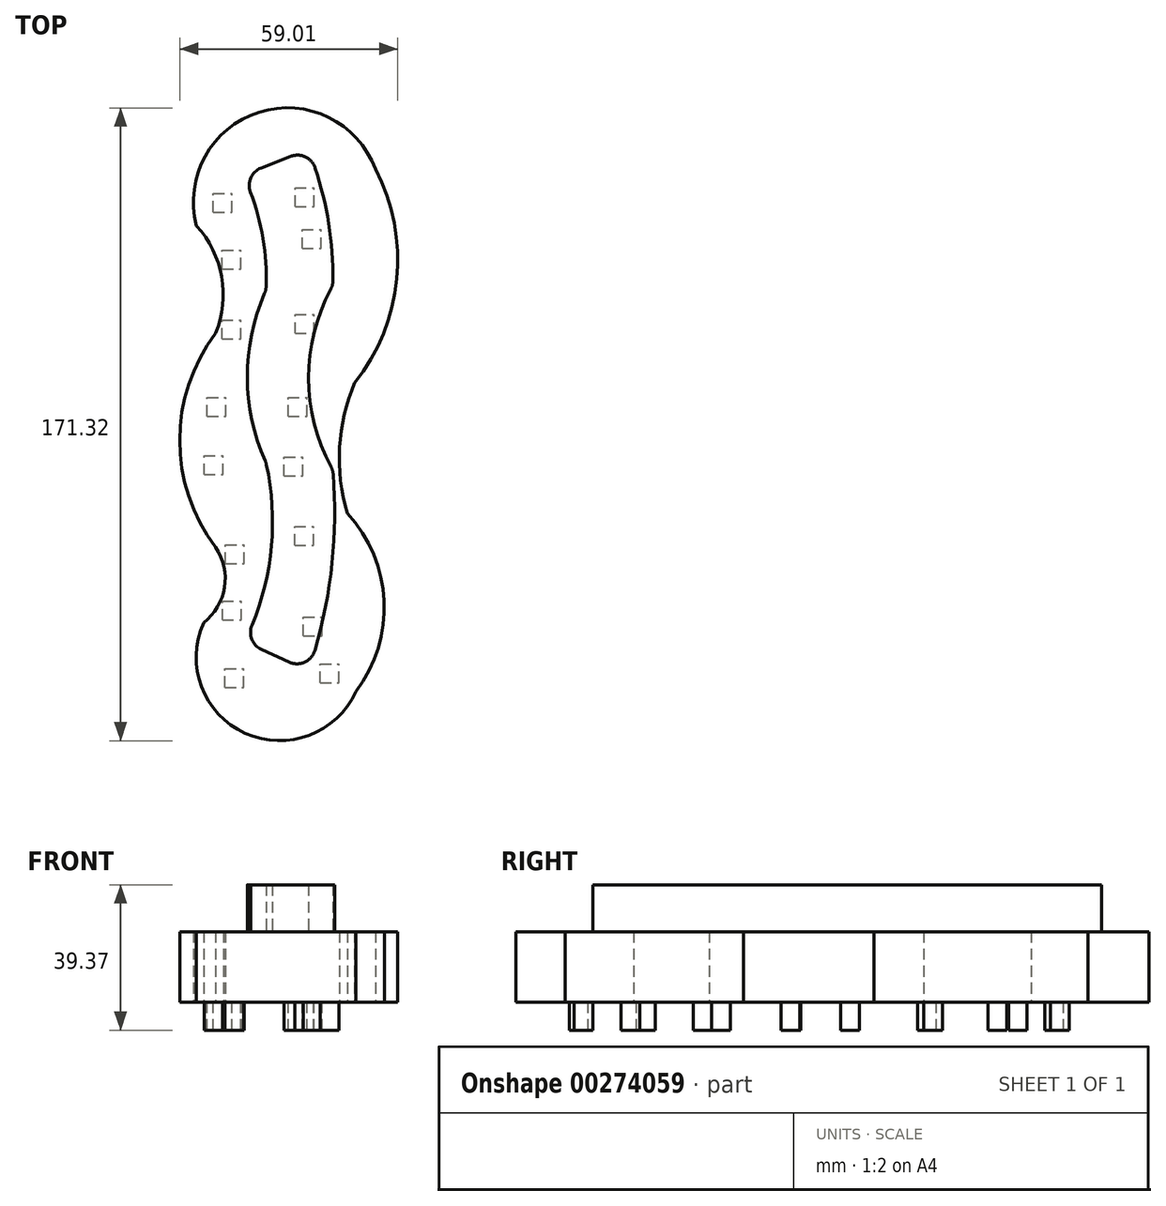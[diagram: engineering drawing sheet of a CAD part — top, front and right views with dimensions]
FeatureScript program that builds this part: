
annotation { "Feature Type Name" : "Feature", "Feature Type Description" : "" }
export const myFeature = defineFeature(function(context is Context, id is Id, definition is map)
    precondition{}
    {
        {
            var Q0;
            Q0=qCreatedBy(makeId("Top.planeOp"),FACE);
            var sketch = newSketch(context, id + "F0", { "sketchPlane" : qUnion([Q0])});
            skLineSegment(sketch, "E0", {"start": v(-34.97, -9.1) * mm, "end": v(6.23, -27.7) * mm});
            skArc(sketch, "E1", {"start": v(-34.97, -9.1) * mm, "mid": v(-29.31, 0.48) * mm, "end": v(-31.68, 11.35) * mm});
            skArc(sketch, "E2", {"start": v(6.23, -27.7) * mm, "mid": v(13.88, -3.14) * mm, "end": v(3.94, 20.58) * mm});
            skLineSegment(sketch, "E3", {"start": v(-31.68, 11.35) * mm, "end": v(3.94, 20.58) * mm});
            skArc(sketch, "E4", {"start": v(-34.97, -9.1) * mm, "mid": v(-23.67, -39) * mm, "end": v(6.23, -27.7) * mm});
            skArc(sketch, "E5", {"start": v(-31.68, 69.27) * mm, "mid": v(-41.43, 40.3) * mm, "end": v(-31.68, 11.35) * mm});
            skLineSegment(sketch, "E6", {"start": v(-31.68, 69.27) * mm, "end": v(5.89, 55.85) * mm});
            skArc(sketch, "E7", {"start": v(5.89, 55.85) * mm, "mid": v(1.82, 38.38) * mm, "end": v(3.94, 20.58) * mm});
            skArc(sketch, "E8", {"start": v(11.52, 113.78) * mm, "mid": v(-19.98, 129.13) * mm, "end": v(-36.89, 98.44) * mm});
            skLineSegment(sketch, "E9", {"start": v(-36.89, 98.44) * mm, "end": v(11.52, 113.78) * mm});
            skArc(sketch, "E10", {"start": v(5.89, 55.85) * mm, "mid": v(17.33, 83.98) * mm, "end": v(11.52, 113.78) * mm});
            skArc(sketch, "E11", {"start": v(-31.68, 69.27) * mm, "mid": v(-30.07, 84.6) * mm, "end": v(-36.89, 98.44) * mm});
            skSolve(sketch);
        }
        {
            var Q0;
            Q0=makeQuery(id+"F0.imprint","IMPRINT",FACE,{"disambiguationData":[TD([[makeQuery(id+"F0.imprint","IMPRINT",EDGE,{"derivedFrom":sQuery(id+"F0.wireOp",EDGE,"E3")}),1.0]])]});
            var Q1;
            Q1=makeQuery(id+"F0.imprint","IMPRINT",FACE,{"disambiguationData":[TD([[makeQuery(id+"F0.imprint","IMPRINT",EDGE,{"derivedFrom":sQuery(id+"F0.wireOp",EDGE,"E6")}),1.0]])]});
            var Q2;
            Q2=makeQuery(id+"F0.imprint","IMPRINT",FACE,{"disambiguationData":[TD([[makeQuery(id+"F0.imprint","IMPRINT",EDGE,{"derivedFrom":sQuery(id+"F0.wireOp",EDGE,"a58SHAlN-x6xV-4BNq-kxud-XYAnyNqKildt")}),1.0]])]});
            var Q3;
            Q3=makeQuery(id+"F0.imprint","IMPRINT",FACE,{"disambiguationData":[TD([[makeQuery(id+"F0.imprint","IMPRINT",EDGE,{"derivedFrom":sQuery(id+"F0.wireOp",EDGE,"E0")}),1.0]])]});
            var Q4;
            Q4=makeQuery(id+"F0.imprint","IMPRINT",FACE,{"disambiguationData":[TD([[makeQuery(id+"F0.imprint","IMPRINT",EDGE,{"derivedFrom":sQuery(id+"F0.wireOp",EDGE,"E0")}),-1.0]])]});
            var Q5;
            Q5=makeQuery(id+"F0.imprint","IMPRINT",FACE,{"disambiguationData":[TD([[makeQuery(id+"F0.imprint","IMPRINT",EDGE,{"derivedFrom":sQuery(id+"F0.wireOp",EDGE,"E8")}),1.0]])]});
            extrude(context, id + "F1", {"entities" : qUnion([Q0, Q1, Q2, Q3, Q4, Q5]), "depth" : 19.05 * mm});
        }
        {
            var Q0;
            Q0=makeQuery(id+"F1.opExtrude","CAP_FACE",FACE,{"disambiguationData":[OSD([sQuery(id+"F0.wireOp",EDGE,"E1"),sQuery(id+"F0.wireOp",EDGE,"E2"),sQuery(id+"F0.wireOp",EDGE,"E4"),sQuery(id+"F0.wireOp",EDGE,"E5"),sQuery(id+"F0.wireOp",EDGE,"E7"),sQuery(id+"F0.wireOp",EDGE,"y8oEunEV-7m8y-mLdO-WgAL-elxjpnqB0Ok1"),sQuery(id+"F0.wireOp",EDGE,"gLmkTJ3O-k5YJ-fcJt-Nht8-fA2oNjS35Pd1"),sQuery(id+"F0.wireOp",EDGE,"th3IJQT3-aCHs-HDTz-tffu-n3fJ1kGaR91I")])],"isStart":false});
            var sketch = newSketch(context, id + "F2", { "sketchPlane" : qUnion([Q0])});
            skLineSegment(sketch, "E12", {"start": v(-23.9, -14.2) * mm, "end": v(-6.6, -22.13) * mm});
            skArc(sketch, "E13", {"start": v(-23.9, -14.2) * mm, "mid": v(-16.83, 9.55) * mm, "end": v(-18.1, 34.3) * mm});
            skArc(sketch, "E14", {"start": v(-6.6, -22.13) * mm, "mid": v(-0.46, 4.74) * mm, "end": v(0, 32.3) * mm});
            skArc(sketch, "E15", {"start": v(-18.1, 80.92) * mm, "mid": v(-23.16, 57.6) * mm, "end": v(-18.1, 34.3) * mm});
            skArc(sketch, "E16", {"start": v(0, 82.21) * mm, "mid": v(-6.55, 57.26) * mm, "end": v(0, 32.3) * mm});
            skArc(sketch, "E17", {"start": v(-18.1, 80.92) * mm, "mid": v(-19.27, 96.9) * mm, "end": v(-24.24, 112.15) * mm});
            skArc(sketch, "E18", {"start": v(0, 82.21) * mm, "mid": v(-1.44, 100.98) * mm, "end": v(-6.6, 119.07) * mm});
            skLineSegment(sketch, "E19", {"start": v(-24.24, 112.15) * mm, "end": v(-6.6, 119.07) * mm});
            skLineSegment(sketch, "E20", {"start": v(0, 32.3) * mm, "end": v(-18.1, 34.3) * mm});
            skSolve(sketch);
        }
        {
            var Q0;
            Q0=makeQuery(id+"F2.imprint","IMPRINT",FACE,{"disambiguationData":[TD([[makeQuery(id+"F2.imprint","IMPRINT",EDGE,{"derivedFrom":sQuery(id+"F2.wireOp",EDGE,"E12")}),1.0]])]});
            var Q1;
            Q1=makeQuery(id+"F2.imprint","IMPRINT",FACE,{"disambiguationData":[TD([[makeQuery(id+"F2.imprint","IMPRINT",EDGE,{"derivedFrom":sQuery(id+"F2.wireOp",EDGE,"E15")}),1.0]])]});
            extrude(context, id + "F3", {"entities" : qUnion([Q0, Q1]), "operationType" : NewBodyOperationType.ADD, "depth" : 12.7 * mm});
        }
        {
            var Q0;
            Q0=makeQuery(id+"F3.opExtrude","SWEPT_EDGE",EDGE,{"disambiguationData":[OSD([sQuery(id+"F2.wireOp",EDGE,"E12"),sQuery(id+"F2.wireOp",EDGE,"E13")])]});
            var Q1;
            Q1=makeQuery(id+"F3.opExtrude","SWEPT_EDGE",EDGE,{"disambiguationData":[OSD([sQuery(id+"F2.wireOp",EDGE,"E12"),sQuery(id+"F2.wireOp",EDGE,"E14")])]});
            var Q2;
            Q2=makeQuery(id+"F3.opExtrude","SWEPT_EDGE",EDGE,{"disambiguationData":[OSD([sQuery(id+"F2.wireOp",EDGE,"E18"),sQuery(id+"F2.wireOp",EDGE,"E19")])]});
            var Q3;
            Q3=makeQuery(id+"F3.opExtrude","SWEPT_EDGE",EDGE,{"disambiguationData":[OSD([sQuery(id+"F2.wireOp",EDGE,"E17"),sQuery(id+"F2.wireOp",EDGE,"E19")])]});
            var Q4;
            Q4=makeQuery(id+"F3.opExtrude","SWEPT_EDGE",EDGE,{"disambiguationData":[OSD([sQuery(id+"F2.wireOp",EDGE,"E16"),sQuery(id+"F2.wireOp",EDGE,"E18")])]});
            var Q5;
            Q5=makeQuery(id+"F3.opExtrude","SWEPT_EDGE",EDGE,{"disambiguationData":[OSD([sQuery(id+"F2.wireOp",EDGE,"E14"),sQuery(id+"F2.wireOp",EDGE,"E16")])]});
            var Q6;
            Q6=makeQuery(id+"F3.opExtrude","SWEPT_EDGE",EDGE,{"disambiguationData":[OSD([sQuery(id+"F2.wireOp",EDGE,"E15"),sQuery(id+"F2.wireOp",EDGE,"E17")])]});
            var Q7;
            Q7=makeQuery(id+"F3.opExtrude","SWEPT_EDGE",EDGE,{"disambiguationData":[OSD([sQuery(id+"F2.wireOp",EDGE,"E13"),sQuery(id+"F2.wireOp",EDGE,"E15")])]});
            fillet(context, id + "F4", {"entities" : qUnion([Q0, Q1, Q2, Q3, Q4, Q5, Q6, Q7]), "radius" : 5.08 * mm, "tangentPropagation" : true, "allowEdgeOverflow" : false});
        }
        {
            var Q0;
            Q0=qCreatedBy(makeId("Top.planeOp"),FACE);
            var sketch = newSketch(context, id + "F5", { "sketchPlane" : qUnion([Q0])});
            skLineSegment(sketch, "E21.bottom", {"start": v(-29.2, -26.6) * mm, "end": v(-24.11, -26.6) * mm});
            skLineSegment(sketch, "E21.top", {"start": v(-29.2, -21.51) * mm, "end": v(-24.11, -21.51) * mm});
            skLineSegment(sketch, "E21.left", {"start": v(-29.2, -26.6) * mm, "end": v(-29.2, -21.51) * mm});
            skLineSegment(sketch, "E21.right", {"start": v(-24.11, -26.6) * mm, "end": v(-24.11, -21.51) * mm});
            skLineSegment(sketch, "E22.bottom", {"start": v(-3.4, -25.27) * mm, "end": v(1.68, -25.27) * mm});
            skLineSegment(sketch, "E22.top", {"start": v(-3.4, -20.19) * mm, "end": v(1.68, -20.19) * mm});
            skLineSegment(sketch, "E22.left", {"start": v(-3.4, -25.27) * mm, "end": v(-3.4, -20.19) * mm});
            skLineSegment(sketch, "E22.right", {"start": v(1.68, -25.27) * mm, "end": v(1.68, -20.19) * mm});
            skLineSegment(sketch, "E23.bottom", {"start": v(-29.86, -8.35) * mm, "end": v(-24.78, -8.35) * mm});
            skLineSegment(sketch, "E23.top", {"start": v(-29.86, -3.27) * mm, "end": v(-24.78, -3.27) * mm});
            skLineSegment(sketch, "E23.left", {"start": v(-29.86, -8.35) * mm, "end": v(-29.86, -3.27) * mm});
            skLineSegment(sketch, "E23.right", {"start": v(-24.78, -8.35) * mm, "end": v(-24.78, -3.27) * mm});
            skLineSegment(sketch, "E24.bottom", {"start": v(-7.97, -12.62) * mm, "end": v(-2.9, -12.62) * mm});
            skLineSegment(sketch, "E24.top", {"start": v(-7.97, -7.54) * mm, "end": v(-2.9, -7.54) * mm});
            skLineSegment(sketch, "E24.left", {"start": v(-7.97, -12.62) * mm, "end": v(-7.97, -7.54) * mm});
            skLineSegment(sketch, "E24.right", {"start": v(-2.9, -12.62) * mm, "end": v(-2.9, -7.54) * mm});
            skLineSegment(sketch, "E25.bottom", {"start": v(-29.06, 6.98) * mm, "end": v(-23.98, 6.98) * mm});
            skLineSegment(sketch, "E25.top", {"start": v(-29.06, 12.06) * mm, "end": v(-23.98, 12.06) * mm});
            skLineSegment(sketch, "E25.left", {"start": v(-29.06, 6.98) * mm, "end": v(-29.06, 12.06) * mm});
            skLineSegment(sketch, "E25.right", {"start": v(-23.98, 6.98) * mm, "end": v(-23.98, 12.06) * mm});
            skLineSegment(sketch, "E26.bottom", {"start": v(-10.3, 11.96) * mm, "end": v(-5.22, 11.96) * mm});
            skLineSegment(sketch, "E26.top", {"start": v(-10.3, 17.04) * mm, "end": v(-5.22, 17.04) * mm});
            skLineSegment(sketch, "E26.left", {"start": v(-10.3, 11.96) * mm, "end": v(-10.3, 17.04) * mm});
            skLineSegment(sketch, "E26.right", {"start": v(-5.22, 11.96) * mm, "end": v(-5.22, 17.04) * mm});
            skLineSegment(sketch, "E27.bottom", {"start": v(-34.83, 31.03) * mm, "end": v(-29.75, 31.03) * mm});
            skLineSegment(sketch, "E27.top", {"start": v(-34.83, 36.1) * mm, "end": v(-29.75, 36.1) * mm});
            skLineSegment(sketch, "E27.left", {"start": v(-34.83, 31.03) * mm, "end": v(-34.83, 36.1) * mm});
            skLineSegment(sketch, "E27.right", {"start": v(-29.75, 31.03) * mm, "end": v(-29.75, 36.1) * mm});
            skLineSegment(sketch, "E28.bottom", {"start": v(-13.17, 30.72) * mm, "end": v(-8.09, 30.72) * mm});
            skLineSegment(sketch, "E28.top", {"start": v(-13.17, 35.8) * mm, "end": v(-8.09, 35.8) * mm});
            skLineSegment(sketch, "E28.left", {"start": v(-13.17, 30.72) * mm, "end": v(-13.17, 35.8) * mm});
            skLineSegment(sketch, "E28.right", {"start": v(-8.09, 30.72) * mm, "end": v(-8.09, 35.8) * mm});
            skLineSegment(sketch, "E29.bottom", {"start": v(-34, 46.87) * mm, "end": v(-28.92, 46.87) * mm});
            skLineSegment(sketch, "E29.top", {"start": v(-34, 51.95) * mm, "end": v(-28.92, 51.95) * mm});
            skLineSegment(sketch, "E29.left", {"start": v(-34, 46.87) * mm, "end": v(-34, 51.95) * mm});
            skLineSegment(sketch, "E29.right", {"start": v(-28.92, 46.87) * mm, "end": v(-28.92, 51.95) * mm});
            skLineSegment(sketch, "E30.bottom", {"start": v(-12.08, 46.83) * mm, "end": v(-7, 46.83) * mm});
            skLineSegment(sketch, "E30.top", {"start": v(-12.08, 51.9) * mm, "end": v(-7, 51.9) * mm});
            skLineSegment(sketch, "E30.left", {"start": v(-12.08, 46.83) * mm, "end": v(-12.08, 51.9) * mm});
            skLineSegment(sketch, "E30.right", {"start": v(-7, 46.83) * mm, "end": v(-7, 51.9) * mm});
            skLineSegment(sketch, "E31.bottom", {"start": v(-30, 67.73) * mm, "end": v(-24.92, 67.73) * mm});
            skLineSegment(sketch, "E31.top", {"start": v(-30, 72.81) * mm, "end": v(-24.92, 72.81) * mm});
            skLineSegment(sketch, "E31.left", {"start": v(-30, 67.73) * mm, "end": v(-30, 72.81) * mm});
            skLineSegment(sketch, "E31.right", {"start": v(-24.92, 67.73) * mm, "end": v(-24.92, 72.81) * mm});
            skLineSegment(sketch, "E32.bottom", {"start": v(-10.19, 69.28) * mm, "end": v(-5.1, 69.28) * mm});
            skLineSegment(sketch, "E32.top", {"start": v(-10.19, 74.36) * mm, "end": v(-5.1, 74.36) * mm});
            skLineSegment(sketch, "E32.left", {"start": v(-10.19, 69.28) * mm, "end": v(-10.19, 74.36) * mm});
            skLineSegment(sketch, "E32.right", {"start": v(-5.1, 69.28) * mm, "end": v(-5.1, 74.36) * mm});
            skLineSegment(sketch, "E33.bottom", {"start": v(-29.97, 86.75) * mm, "end": v(-24.89, 86.75) * mm});
            skLineSegment(sketch, "E33.top", {"start": v(-29.97, 91.83) * mm, "end": v(-24.89, 91.83) * mm});
            skLineSegment(sketch, "E33.left", {"start": v(-29.97, 86.75) * mm, "end": v(-29.97, 91.83) * mm});
            skLineSegment(sketch, "E33.right", {"start": v(-24.89, 86.75) * mm, "end": v(-24.89, 91.83) * mm});
            skLineSegment(sketch, "E34.bottom", {"start": v(-8.3, 92.25) * mm, "end": v(-3.21, 92.25) * mm});
            skLineSegment(sketch, "E34.top", {"start": v(-8.3, 97.33) * mm, "end": v(-3.21, 97.33) * mm});
            skLineSegment(sketch, "E34.left", {"start": v(-8.3, 92.25) * mm, "end": v(-8.3, 97.33) * mm});
            skLineSegment(sketch, "E34.right", {"start": v(-3.21, 92.25) * mm, "end": v(-3.21, 97.33) * mm});
            skLineSegment(sketch, "E35.bottom", {"start": v(-32.31, 102.08) * mm, "end": v(-27.23, 102.08) * mm});
            skLineSegment(sketch, "E35.top", {"start": v(-32.31, 107.16) * mm, "end": v(-27.23, 107.16) * mm});
            skLineSegment(sketch, "E35.left", {"start": v(-32.31, 102.08) * mm, "end": v(-32.31, 107.16) * mm});
            skLineSegment(sketch, "E35.right", {"start": v(-27.23, 102.08) * mm, "end": v(-27.23, 107.16) * mm});
            skLineSegment(sketch, "E36.bottom", {"start": v(-10.19, 103.6) * mm, "end": v(-5.1, 103.6) * mm});
            skLineSegment(sketch, "E36.top", {"start": v(-10.19, 108.68) * mm, "end": v(-5.1, 108.68) * mm});
            skLineSegment(sketch, "E36.left", {"start": v(-10.19, 103.6) * mm, "end": v(-10.19, 108.68) * mm});
            skLineSegment(sketch, "E36.right", {"start": v(-5.1, 103.6) * mm, "end": v(-5.1, 108.68) * mm});
            skSolve(sketch);
        }
        {
            var Q0;
            Q0 = qSketchRegion(id + "F5", true);
            extrude(context, id + "F6", {"entities" : qUnion([Q0]), "operationType" : NewBodyOperationType.ADD, "oppositeDirection" : true, "depth" : 7.62 * mm});
        }
    });
